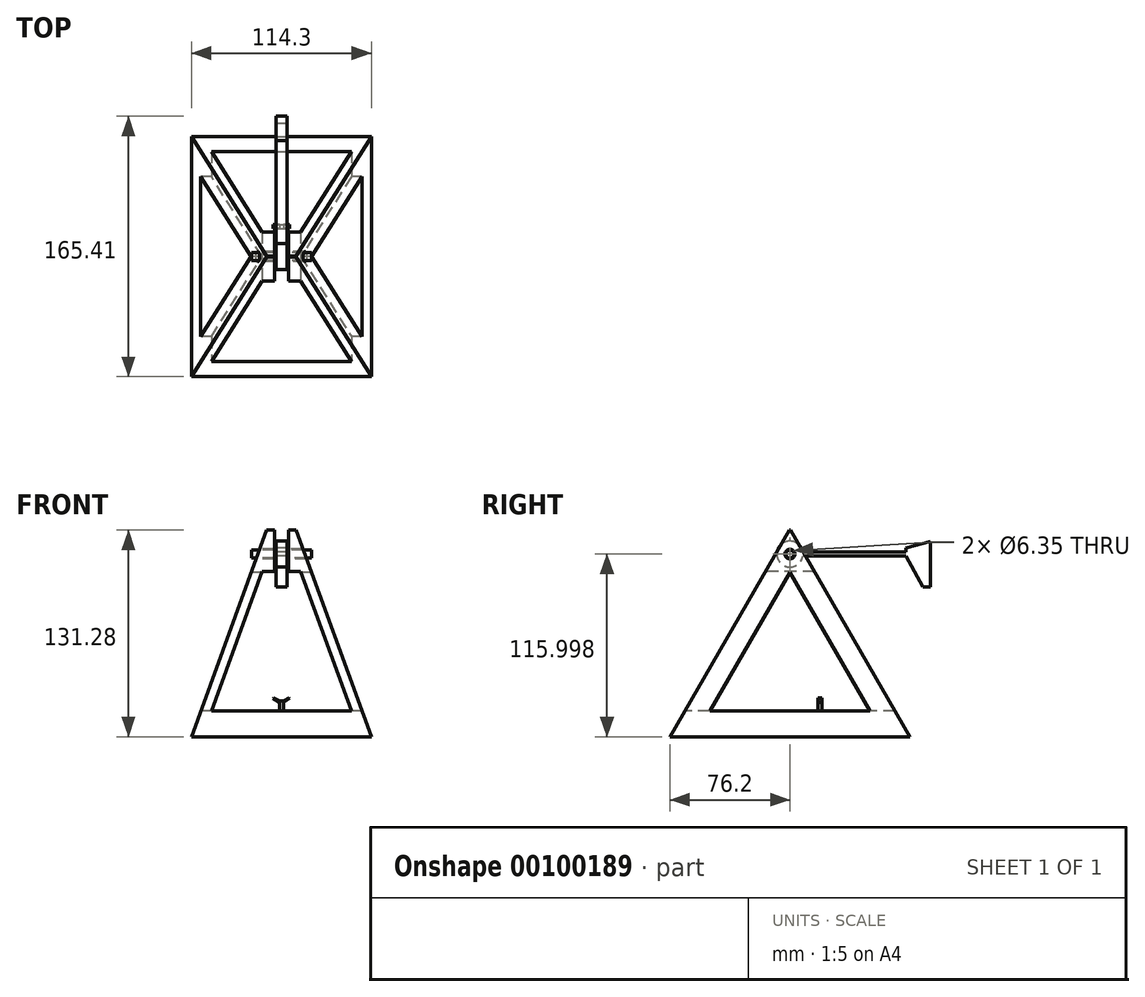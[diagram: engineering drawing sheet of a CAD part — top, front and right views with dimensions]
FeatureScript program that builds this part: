
annotation { "Feature Type Name" : "Feature", "Feature Type Description" : "" }
export const myFeature = defineFeature(function(context is Context, id is Id, definition is map)
    precondition{}
    {
        {
            var Q0;
            Q0=qCreatedBy(makeId("Right.planeOp"),FACE);
            var sketch = newSketch(context, id + "F0", { "sketchPlane" : qUnion([Q0])});
            skLineSegment(sketch, "E0", {"start": v(0, 0) * mm, "end": v(0, 131.98) * mm, "construction": true});
            skLineSegment(sketch, "E1", {"start": v(0, 131.98) * mm, "end": v(-76.2, 0) * mm});
            skLineSegment(sketch, "E2", {"start": v(-76.2, 0) * mm, "end": v(76.2, 0) * mm});
            skLineSegment(sketch, "E3", {"start": v(76.2, 0) * mm, "end": v(0, 131.98) * mm});
            skLineSegment(sketch, "E4", {"start": v(-50.8, 16.33) * mm, "end": v(50.8, 16.33) * mm});
            skLineSegment(sketch, "E5", {"start": v(50.8, 16.33) * mm, "end": v(0, 104.32) * mm});
            skLineSegment(sketch, "E6", {"start": v(0, 104.32) * mm, "end": v(-50.8, 16.33) * mm});
            skCircle(sketch, "E7", {"center": v(0, 116) * mm, "radius": 3.18 * mm});
            skSolve(sketch);
        }
        {
            var Q0;
            Q0=qCreatedBy(makeId("Front.planeOp"),FACE);
            var sketch = newSketch(context, id + "F1", { "sketchPlane" : qUnion([Q0])});
            skLineSegment(sketch, "E8", {"start": v(0, 0) * mm, "end": v(0, 131.28) * mm, "construction": true});
            skLineSegment(sketch, "E9", {"start": v(-57.15, 0) * mm, "end": v(57.15, 0) * mm});
            skLineSegment(sketch, "E10", {"start": v(-9.37, 131.28) * mm, "end": v(9.37, 131.28) * mm});
            skLineSegment(sketch, "E11", {"start": v(-57.15, 0) * mm, "end": v(-9.37, 131.28) * mm});
            skLineSegment(sketch, "E12", {"start": v(9.37, 131.28) * mm, "end": v(57.15, 0) * mm});
            skLineSegment(sketch, "E13", {"start": v(-44.45, 16.33) * mm, "end": v(-12.23, 104.86) * mm});
            skLineSegment(sketch, "E14", {"start": v(12.23, 104.86) * mm, "end": v(44.45, 16.33) * mm});
            skLineSegment(sketch, "E15", {"start": v(44.45, 16.33) * mm, "end": v(-44.45, 16.33) * mm});
            skPoint(sketch, "E16", {"position": v(0, 16.33) * mm});
            skLineSegment(sketch, "E17", {"start": v(0, 131.28) * mm, "end": v(0, 104.86) * mm});
            skLineSegment(sketch, "E18", {"start": v(-12.23, 104.86) * mm, "end": v(12.23, 104.86) * mm});
            skLineSegment(sketch, "E19", {"start": v(-4.45, 131.28) * mm, "end": v(-4.44, 104.86) * mm});
            skLineSegment(sketch, "E20", {"start": v(4.45, 104.86) * mm, "end": v(4.45, 131.28) * mm});
            skSolve(sketch);
        }
        {
            var Q0;
            Q0=makeQuery(id+"F1.imprint","IMPRINT",FACE,{"disambiguationData":[TD([[makeQuery(id+"F1.imprint","IMPRINT",EDGE,{"derivedFrom":sQuery(id+"F1.wireOp",EDGE,"E9")}),1.0]])]});
            extrude(context, id + "F2", {"entities" : qUnion([Q0]), "endBound" : BoundingType.SYMMETRIC, "oppositeDirection" : true, "depth" : 152.4 * mm});
        }
        {
            var Q0;
            Q0=makeQuery(id+"F0.imprint","IMPRINT",FACE,{"disambiguationData":[TD([[makeQuery(id+"F0.imprint","IMPRINT",EDGE,{"derivedFrom":sQuery(id+"F0.wireOp",EDGE,"E1")}),1.0]])]});
            extrude(context, id + "F3", {"entities" : qUnion([Q0]), "operationType" : NewBodyOperationType.INTERSECT, "endBound" : BoundingType.SYMMETRIC, "depth" : 114.3 * mm});
        }
        {
            var Q0;
            Q0=makeQuery(id+"F0.imprint","IMPRINT",FACE,{"disambiguationData":[TD([[makeQuery(id+"F0.imprint","IMPRINT",EDGE,{"derivedFrom":sQuery(id+"F0.wireOp",EDGE,"E1")}),1.0]])]});
            var sketch = newSketch(context, id + "F4", { "sketchPlane" : qUnion([Q0])});
            skLineSegment(sketch, "E21", {"start": v(0, 0) * mm, "end": v(0, 116) * mm, "construction": true});
            skCircle(sketch, "E22", {"center": v(0, 116) * mm, "radius": 2.54 * mm});
            skSolve(sketch);
        }
        {
            var Q0;
            Q0 = qSketchRegion(id + "F4", true);
            extrude(context, id + "F5", {"entities" : qUnion([Q0]), "endBound" : BoundingType.SYMMETRIC, "depth" : 38.1 * mm});
        }
        {
            var Q0;
            Q0=makeQuery(id+"F0.imprint","IMPRINT",FACE,{"disambiguationData":[TD([[makeQuery(id+"F0.imprint","IMPRINT",EDGE,{"derivedFrom":sQuery(id+"F0.wireOp",EDGE,"E7")}),1.0]])]});
            var sketch = newSketch(context, id + "F6", { "sketchPlane" : qUnion([Q0])});
            skLineSegment(sketch, "E23", {"start": v(0, 0) * mm, "end": v(0, 116) * mm, "construction": true});
            skCircle(sketch, "E24", {"center": v(0, 116) * mm, "radius": 8.26 * mm});
            skLineSegment(sketch, "E25", {"start": v(0, 116) * mm, "end": v(89.2, 116) * mm});
            skLineSegment(sketch, "E26", {"start": v(0, 114.73) * mm, "end": v(89.2, 114.73) * mm});
            skLineSegment(sketch, "E27", {"start": v(89.2, 114.73) * mm, "end": v(89.2, 117.27) * mm});
            skLineSegment(sketch, "E28", {"start": v(89.2, 117.27) * mm, "end": v(0, 117.27) * mm});
            skLineSegment(sketch, "E29", {"start": v(0, 117.27) * mm, "end": v(0, 116) * mm});
            skLineSegment(sketch, "E30", {"start": v(89.2, 114.73) * mm, "end": v(89.2, 95.08) * mm});
            skLineSegment(sketch, "E31", {"start": v(89.2, 95.08) * mm, "end": v(84.34, 95.08) * mm});
            skLineSegment(sketch, "E32", {"start": v(84.34, 95.08) * mm, "end": v(73.69, 114.73) * mm});
            skLineSegment(sketch, "E33", {"start": v(73.69, 114.73) * mm, "end": v(73.69, 119.8) * mm});
            skLineSegment(sketch, "E34", {"start": v(89.2, 117.27) * mm, "end": v(89.2, 123.97) * mm});
            skLineSegment(sketch, "E35", {"start": v(89.2, 123.97) * mm, "end": v(73.69, 119.8) * mm});
            skLineSegment(sketch, "E36", {"start": v(89.2, 123.97) * mm, "end": v(57.5, 123.97) * mm, "construction": true});
            skSolve(sketch);
        }
        {
            var Q0;
            Q0 = qSketchRegion(id + "F6", true);
            extrude(context, id + "F7", {"entities" : qUnion([Q0]), "operationType" : NewBodyOperationType.ADD, "endBound" : BoundingType.SYMMETRIC, "depth" : 7 * mm});
        }
        {
            var Q0;
            {var subQ1=sQuery(id+"F1.wireOp",EDGE,"E13");Q0=makeQuery(id+"F1.imprint","IMPRINT",FACE,{"disambiguationData":[TD([[makeQuery(id+"F1.imprint","IMPRINT",EDGE,{"derivedFrom":subQ1}),-1.0]])]});}
            var sketch = newSketch(context, id + "F8", { "sketchPlane" : qUnion([Q0])});
            skLineSegment(sketch, "E37", {"start": v(0, 0) * mm, "end": v(0, 22.68) * mm, "construction": true});
            skLineSegment(sketch, "E38", {"start": v(0, 22.68) * mm, "end": v(1.27, 22.68) * mm});
            skLineSegment(sketch, "E39", {"start": v(1.27, 22.68) * mm, "end": v(1.27, 16.33) * mm});
            skLineSegment(sketch, "E40", {"start": v(1.27, 16.33) * mm, "end": v(-1.27, 16.33) * mm});
            skLineSegment(sketch, "E41", {"start": v(-1.27, 16.33) * mm, "end": v(-1.27, 22.68) * mm});
            skLineSegment(sketch, "E42", {"start": v(-1.27, 22.68) * mm, "end": v(0, 22.68) * mm});
            skLineSegment(sketch, "E43", {"start": v(-1.27, 22.68) * mm, "end": v(-4.9, 24.77) * mm});
            skLineSegment(sketch, "E44", {"start": v(-4.9, 24.77) * mm, "end": v(-5.21, 24.22) * mm});
            skLineSegment(sketch, "E45", {"start": v(-5.21, 24.22) * mm, "end": v(-1.27, 21.95) * mm});
            skLineSegment(sketch, "E46.MirrorCS", {"start": v(1.27, 22.68) * mm, "end": v(4.9, 24.77) * mm});
            skLineSegment(sketch, "E47.MirrorCS", {"start": v(5.21, 24.22) * mm, "end": v(1.27, 21.95) * mm});
            skLineSegment(sketch, "E48.MirrorCS", {"start": v(4.9, 24.77) * mm, "end": v(5.21, 24.22) * mm});
            skSolve(sketch);
        }
        {
            var Q0;
            Q0 = qSketchRegion(id + "F8", true);
            extrude(context, id + "F9", {"entities" : qUnion([Q0]), "oppositeDirection" : true, "depth" : 20.32 * mm, "hasSecondDirection" : true, "secondDirectionOppositeDirection" : true, "secondDirectionDepth" : 17.78 * mm});
        }
    });
